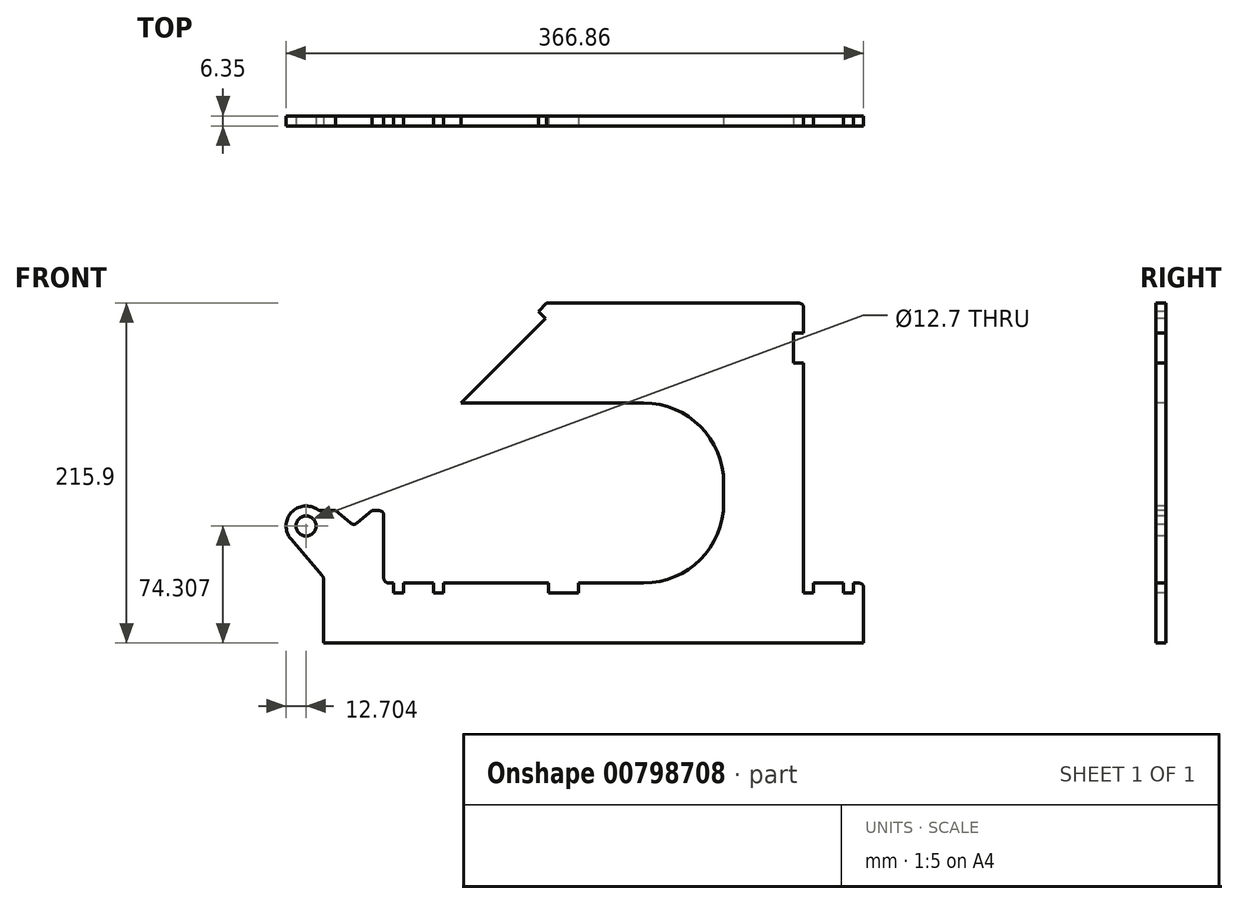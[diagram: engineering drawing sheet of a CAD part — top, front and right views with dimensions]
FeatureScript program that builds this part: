
annotation { "Feature Type Name" : "Feature", "Feature Type Description" : "" }
export const myFeature = defineFeature(function(context is Context, id is Id, definition is map)
    precondition{}
    {
        {
            var Q0;
            Q0=qCreatedBy(makeId("Front.planeOp"),FACE);
            var sketch = newSketch(context, id + "F0", { "sketchPlane" : qUnion([Q0])});
            skCircle(sketch, "E0", {"center": v(-91.4, -60.1) * mm, "radius": 6.35 * mm});
            skArc(sketch, "E1", {"start": v(-83.36, -50.27) * mm, "mid": v(-100.48, -51.22) * mm, "end": v(-101.06, -68.36) * mm});
            skLineSegment(sketch, "E2", {"start": v(-101.06, -68.36) * mm, "end": v(-80.15, -92.8) * mm});
            skLineSegment(sketch, "E3.trimOffspring", {"start": v(-80.15, -92.8) * mm, "end": v(-80.15, -134.4) * mm});
            skCircle(sketch, "E4", {"center": v(-61.1, -45.5) * mm, "radius": 11.11 * mm, "construction": true});
            skLineSegment(sketch, "E5.0", {"start": v(-83.36, -50.27) * mm, "end": v(-72.7, -50.27) * mm});
            skLineSegment(sketch, "E6", {"start": v(-42.05, -50.27) * mm, "end": v(-42.05, -96.3) * mm});
            skLineSegment(sketch, "E7.trimOffspring", {"start": v(-49.48, -50.27) * mm, "end": v(-42.05, -50.27) * mm});
            skPoint(sketch, "E8.orphan", {"position": v(-61.1, -63.47) * mm});
            skLineSegment(sketch, "E9.0", {"start": v(-72.7, -50.27) * mm, "end": v(-61.1, -60.02) * mm});
            skLineSegment(sketch, "E10.0", {"start": v(-49.48, -50.27) * mm, "end": v(-61.1, -60.02) * mm});
            skLineSegment(sketch, "E11", {"start": v(-68.24, -54.02) * mm, "end": v(-61.1, -45.5) * mm, "construction": true});
            skLineSegment(sketch, "E12", {"start": v(-53.95, -54.02) * mm, "end": v(-61.1, -45.5) * mm, "construction": true});
            skLineSegment(sketch, "E13.0", {"start": v(-42.05, -96.3) * mm, "end": v(-35.7, -96.3) * mm});
            skLineSegment(sketch, "E14.0", {"start": v(-80.15, -134.4) * mm, "end": v(262.75, -134.4) * mm});
            skLineSegment(sketch, "E15", {"start": v(-61.1, -45.5) * mm, "end": v(-34.5, -18.92) * mm, "construction": true});
            skLineSegment(sketch, "E16.0", {"start": v(-60.66, -29.36) * mm, "end": v(50.47, 81.77) * mm, "construction": true});
            skLineSegment(sketch, "E17", {"start": v(-61.1, -45.5) * mm, "end": v(-68.95, -37.65) * mm});
            skLineSegment(sketch, "E18.0", {"start": v(-53.24, -37.65) * mm, "end": v(-61.1, -29.8) * mm, "construction": true});
            skLineSegment(sketch, "E19.0", {"start": v(60.57, 71.67) * mm, "end": v(56.08, 76.16) * mm});
            skLineSegment(sketch, "E20.0", {"start": v(-52.8, -37.22) * mm, "end": v(-60.66, -29.36) * mm, "construction": true});
            skLineSegment(sketch, "E21.0", {"start": v(-63.34, -43.26) * mm, "end": v(50.52, 70.6) * mm, "construction": true});
            skLineSegment(sketch, "E22.0", {"start": v(173.85, -32.8) * mm, "end": v(173.85, -45.5) * mm});
            skLineSegment(sketch, "E23.0", {"start": v(61.41, 81.5) * mm, "end": v(224.65, 81.5) * mm});
            skLineSegment(sketch, "E24.0", {"start": v(6.9, 18) * mm, "end": v(123.05, 18) * mm});
            skLineSegment(sketch, "E25.0", {"start": v(224.65, 81.5) * mm, "end": v(224.65, 62.44) * mm});
            skLineSegment(sketch, "E26.0", {"start": v(-23.62, -12.52) * mm, "end": v(6.9, 18) * mm, "construction": true});
            skLineSegment(sketch, "E27.0", {"start": v(-23.62, -12.52) * mm, "end": v(-28.11, -8.03) * mm, "construction": true});
            skLineSegment(sketch, "E28", {"start": v(56.08, 76.16) * mm, "end": v(61.41, 81.5) * mm});
            skLineSegment(sketch, "E29", {"start": v(6.9, 18) * mm, "end": v(60.57, 71.67) * mm});
            skLineSegment(sketch, "E30.top", {"start": v(-35.7, -102.66) * mm, "end": v(-29.35, -102.66) * mm});
            skLineSegment(sketch, "E30.left", {"start": v(-35.7, -96.3) * mm, "end": v(-35.7, -102.66) * mm});
            skLineSegment(sketch, "E30.right", {"start": v(-29.35, -96.3) * mm, "end": v(-29.35, -102.66) * mm});
            skLineSegment(sketch, "E31.bottom", {"start": v(-10.3, -102.66) * mm, "end": v(-3.95, -102.66) * mm});
            skLineSegment(sketch, "E31.left", {"start": v(-10.3, -102.66) * mm, "end": v(-10.3, -96.3) * mm});
            skLineSegment(sketch, "E31.right", {"start": v(-3.95, -102.66) * mm, "end": v(-3.95, -96.3) * mm});
            skLineSegment(sketch, "E32.trimOffspring", {"start": v(-29.35, -96.3) * mm, "end": v(-10.3, -96.3) * mm});
            skLineSegment(sketch, "E33.trimOffspring", {"start": v(-3.95, -96.3) * mm, "end": v(123.05, -96.3) * mm});
            skLineSegment(sketch, "E34.top", {"start": v(224.65, 62.44) * mm, "end": v(218.3, 62.44) * mm});
            skLineSegment(sketch, "E35.bottom", {"start": v(218.3, 43.4) * mm, "end": v(224.65, 43.4) * mm});
            skLineSegment(sketch, "E35.left", {"start": v(218.3, 62.44) * mm, "end": v(218.3, 43.4) * mm});
            skLineSegment(sketch, "E36.trimOffspring", {"start": v(224.65, 43.4) * mm, "end": v(224.65, -102.66) * mm});
            skLineSegment(sketch, "E37.0", {"start": v(262.75, -96.3) * mm, "end": v(262.75, -134.4) * mm});
            skLineSegment(sketch, "E38.trimOffspring", {"start": v(231, -96.3) * mm, "end": v(250.05, -96.3) * mm});
            skLineSegment(sketch, "E39.top", {"start": v(224.65, -102.66) * mm, "end": v(231, -102.66) * mm});
            skLineSegment(sketch, "E39.right", {"start": v(231, -96.3) * mm, "end": v(231, -102.66) * mm});
            skLineSegment(sketch, "E40.top", {"start": v(250.05, -102.66) * mm, "end": v(256.4, -102.66) * mm});
            skLineSegment(sketch, "E40.left", {"start": v(250.05, -96.3) * mm, "end": v(250.05, -102.66) * mm});
            skLineSegment(sketch, "E40.right", {"start": v(256.4, -96.3) * mm, "end": v(256.4, -102.66) * mm});
            skLineSegment(sketch, "E41.trimOffspring", {"start": v(256.4, -96.3) * mm, "end": v(262.75, -96.3) * mm});
            skPoint(sketch, "E42.visualSharp", {"position": v(173.85, 18) * mm});
            skArc(sketch, "E42.filletArc", {"start": v(173.85, -32.8) * mm, "mid": v(158.97, 3.11) * mm, "end": v(123.05, 18) * mm});
            skPoint(sketch, "E43.visualSharp", {"position": v(173.85, -96.3) * mm});
            skArc(sketch, "E43.filletArc", {"start": v(123.05, -96.3) * mm, "mid": v(158.97, -81.43) * mm, "end": v(173.85, -45.5) * mm});
            skLineSegment(sketch, "E44.bottom", {"start": v(62.73, -102.66) * mm, "end": v(81.78, -102.66) * mm});
            skLineSegment(sketch, "E44.top", {"start": v(62.73, -96.3) * mm, "end": v(81.78, -96.3) * mm});
            skLineSegment(sketch, "E44.left", {"start": v(62.73, -102.66) * mm, "end": v(62.73, -96.3) * mm});
            skLineSegment(sketch, "E44.right", {"start": v(81.78, -102.66) * mm, "end": v(81.78, -96.3) * mm});
            skSolve(sketch);
        }
        {
            var Q0;
            Q0=makeQuery(id+"F0.imprint","IMPRINT",FACE,{"disambiguationData":[TD([[makeQuery(id+"F0.imprint","IMPRINT",EDGE,{"derivedFrom":sQuery(id+"F0.wireOp",EDGE,"E0")}),-1.0]])]});
            extrude(context, id + "F1", {"entities" : qUnion([Q0]), "oppositeDirection" : true, "depth" : 6.35 * mm, "offsetDistance" : 25.4 * mm});
        }
        {
            var Q0;
            Q0=makeQuery(id+"F1.opExtrude","SWEPT_EDGE",EDGE,{"disambiguationData":[OSD([sQuery(id+"F0.wireOp",EDGE,"E23.0"),sQuery(id+"F0.wireOp",EDGE,"E25.0")])]});
            var Q1;
            Q1=makeQuery(id+"F1.opExtrude","SWEPT_EDGE",EDGE,{"disambiguationData":[OSD([sQuery(id+"F0.wireOp",EDGE,"E6"),sQuery(id+"F0.wireOp",EDGE,"E13.0")])]});
            fillet(context, id + "F2", {"entities" : qUnion([Q0, Q1]), "radius" : 3.17 * mm, "tangentPropagation" : true, "allowEdgeOverflow" : false});
        }
        {
            var Q0;
            Q0=makeQuery(id+"F1.opExtrude","SWEPT_EDGE",EDGE,{"disambiguationData":[OSD([sQuery(id+"F0.wireOp",EDGE,"E2"),sQuery(id+"F0.wireOp",EDGE,"E3.trimOffspring")])]});
            fillet(context, id + "F3", {"entities" : qUnion([Q0]), "radius" : 5.08 * mm, "tangentPropagation" : true, "allowEdgeOverflow" : false});
        }
        {
            var Q0;
            Q0=makeQuery(id+"F1.opExtrude","SWEPT_EDGE",EDGE,{"disambiguationData":[OSD([sQuery(id+"F0.wireOp",EDGE,"E6"),sQuery(id+"F0.wireOp",EDGE,"E7.trimOffspring")])]});
            fillet(context, id + "F4", {"entities" : qUnion([Q0]), "radius" : 3.17 * mm, "tangentPropagation" : true, "allowEdgeOverflow" : false});
        }
        {
            var Q0;
            Q0=makeQuery(id+"F1.opExtrude","SWEPT_EDGE",EDGE,{"disambiguationData":[OSD([sQuery(id+"F0.wireOp",EDGE,"E9.0"),sQuery(id+"F0.wireOp",EDGE,"E10.0")])]});
            var Q1;
            Q1=makeQuery(id+"F1.opExtrude","SWEPT_EDGE",EDGE,{"disambiguationData":[OSD([sQuery(id+"F0.wireOp",EDGE,"E1"),sQuery(id+"F0.wireOp",EDGE,"E5.0")])]});
            var Q2;
            Q2=makeQuery(id+"F1.opExtrude","SWEPT_EDGE",EDGE,{"disambiguationData":[OSD([sQuery(id+"F0.wireOp",EDGE,"E37.0"),sQuery(id+"F0.wireOp",EDGE,"E41.trimOffspring")])]});
            fillet(context, id + "F5", {"entities" : qUnion([Q0, Q1, Q2]), "radius" : 3.17 * mm, "tangentPropagation" : true, "allowEdgeOverflow" : false});
        }
    });
